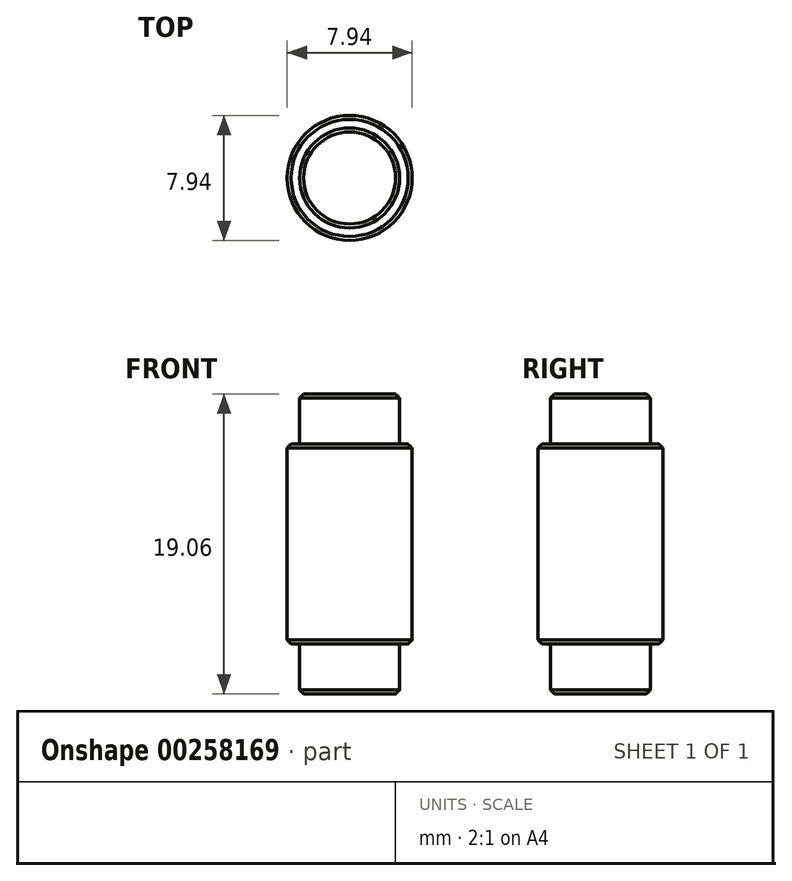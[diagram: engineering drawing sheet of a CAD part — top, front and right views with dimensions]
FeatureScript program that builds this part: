
annotation { "Feature Type Name" : "Feature", "Feature Type Description" : "" }
export const myFeature = defineFeature(function(context is Context, id is Id, definition is map)
    precondition{}
    {
        {
            var Q0;
            Q0=qCreatedBy(makeId("Top.planeOp"),FACE);
            var sketch = newSketch(context, id + "F0", { "sketchPlane" : qUnion([Q0])});
            skCircle(sketch, "E0", {"center": v(0, 0) * mm, "radius": 3.97 * mm});
            skSolve(sketch);
        }
        {
            var Q0;
            Q0=makeQuery(id+"F0.imprint","IMPRINT",FACE,{"disambiguationData":[TD([[makeQuery(id+"F0.imprint","IMPRINT",EDGE,{"derivedFrom":sQuery(id+"F0.wireOp",EDGE,"E0")}),1.0]])]});
            extrude(context, id + "F1", {"entities" : qUnion([Q0]), "depth" : 12.7 * mm});
        }
        {
            var Q0;
            Q0=qCreatedBy(makeId("Top.planeOp"),FACE);
            var sketch = newSketch(context, id + "F2", { "sketchPlane" : qUnion([Q0])});
            skCircle(sketch, "E1", {"center": v(0, 0) * mm, "radius": 3.18 * mm});
            skSolve(sketch);
        }
        {
            var Q0;
            Q0 = qSketchRegion(id + "F2", true);
            extrude(context, id + "F3", {"entities" : qUnion([Q0]), "operationType" : NewBodyOperationType.ADD, "oppositeDirection" : true, "depth" : 3.17 * mm});
        }
        {
            var Q0;
            Q0=makeQuery(id+"F1.opExtrude","CAP_FACE",FACE,{"disambiguationData":[OSD([sQuery(id+"F0.wireOp",EDGE,"E0")])],"isStart":false});
            var sketch = newSketch(context, id + "F4", { "sketchPlane" : qUnion([Q0])});
            skCircle(sketch, "E2", {"center": v(0, 0) * mm, "radius": 3.18 * mm});
            skSolve(sketch);
        }
        {
            var Q0;
            Q0 = qSketchRegion(id + "F4", true);
            extrude(context, id + "F5", {"entities" : qUnion([Q0]), "operationType" : NewBodyOperationType.ADD, "depth" : 3.17 * mm});
        }
        {
            var Q0;
            Q0=makeQuery(id+"F5.opExtrude","CAP_EDGE",EDGE,{"disambiguationData":[OSD([sQuery(id+"F4.wireOp",EDGE,"E2")])],"isStart":false});
            var Q1;
            Q1=makeQuery(id+"F1.opExtrude","CAP_EDGE",EDGE,{"disambiguationData":[OSD([sQuery(id+"F0.wireOp",EDGE,"E0")])],"isStart":false});
            var Q2;
            Q2=makeQuery(id+"F1.opExtrude","CAP_EDGE",EDGE,{"disambiguationData":[OSD([sQuery(id+"F0.wireOp",EDGE,"E0")])],"isStart":true});
            var Q3;
            Q3=makeQuery(id+"F3.opExtrude","CAP_EDGE",EDGE,{"disambiguationData":[OSD([sQuery(id+"F2.wireOp",EDGE,"E1")])],"isStart":false});
            chamfer(context, id + "F6", {"entities" : qUnion([Q0, Q1, Q2, Q3]), "width" : 0.25 * mm, "tangentPropagation" : true});
        }
    });
